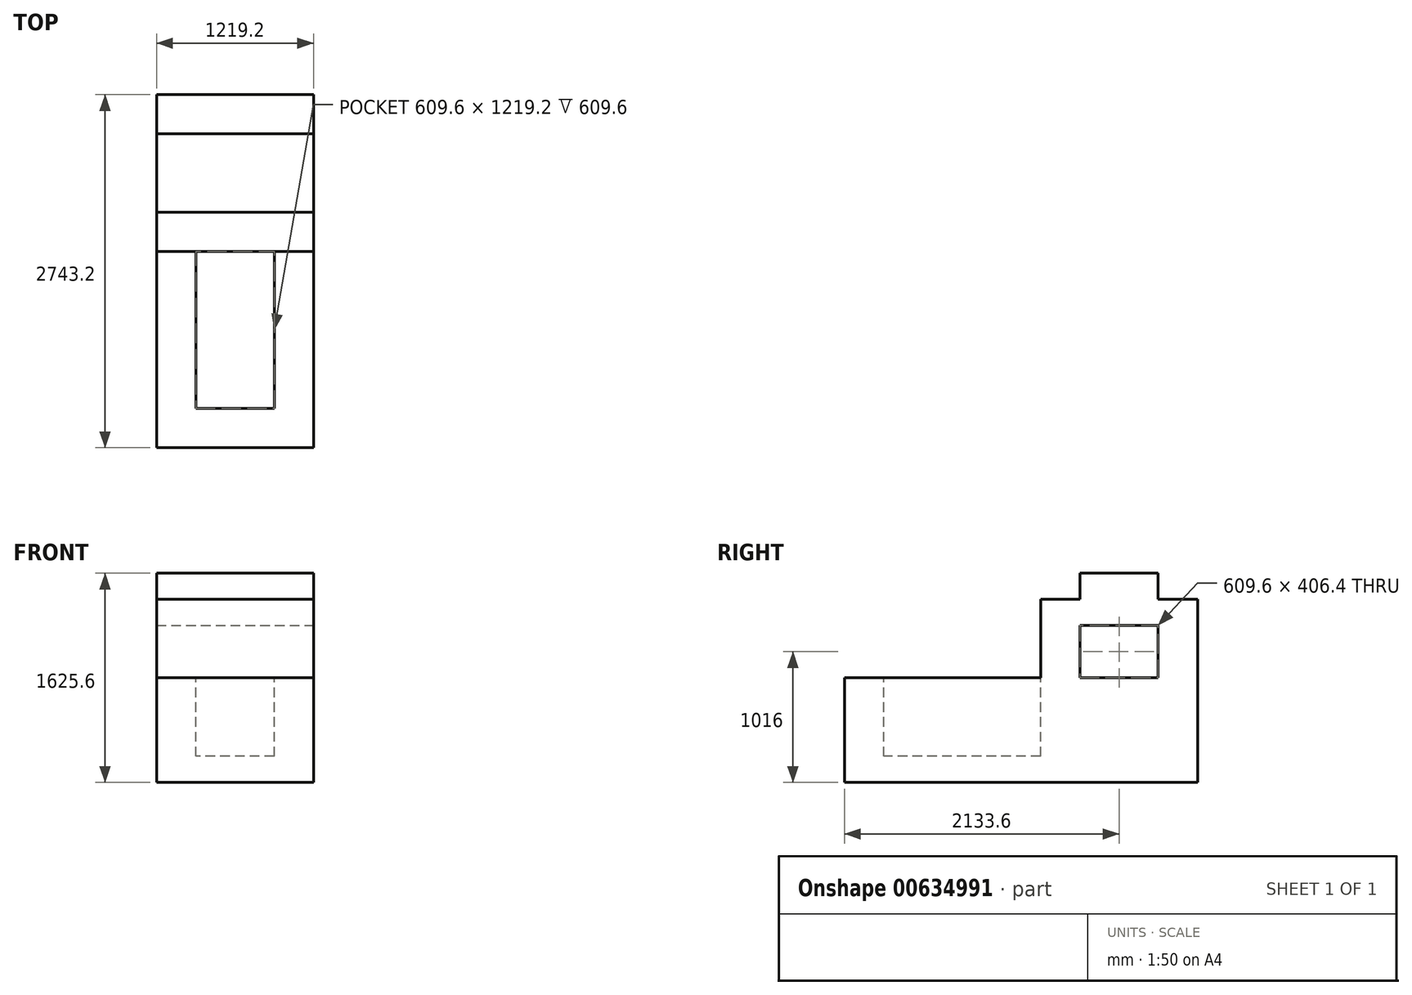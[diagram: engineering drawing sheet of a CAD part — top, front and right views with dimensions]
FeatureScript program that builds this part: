
annotation { "Feature Type Name" : "Feature", "Feature Type Description" : "" }
export const myFeature = defineFeature(function(context is Context, id is Id, definition is map)
    precondition{}
    {
        {
            var Q0;
            Q0=qCreatedBy(makeId("Right.planeOp"),FACE);
            var sketch = newSketch(context, id + "F0", { "sketchPlane" : qUnion([Q0])});
            skLineSegment(sketch, "E0", {"start": v(-227.36, -85.91) * mm, "end": v(2515.84, -85.91) * mm});
            skLineSegment(sketch, "E1", {"start": v(2515.84, -85.91) * mm, "end": v(2515.84, 1336.49) * mm});
            skLineSegment(sketch, "E2", {"start": v(2515.84, 1336.49) * mm, "end": v(2211.04, 1336.49) * mm});
            skLineSegment(sketch, "E3", {"start": v(2211.04, 1336.49) * mm, "end": v(2211.04, 1539.69) * mm});
            skLineSegment(sketch, "E4", {"start": v(2211.04, 1539.69) * mm, "end": v(1601.44, 1539.69) * mm});
            skLineSegment(sketch, "E5", {"start": v(1601.44, 1539.69) * mm, "end": v(1601.44, 1336.49) * mm});
            skLineSegment(sketch, "E6", {"start": v(1601.44, 1336.49) * mm, "end": v(1296.64, 1336.49) * mm});
            skLineSegment(sketch, "E7", {"start": v(1296.64, 1336.49) * mm, "end": v(1296.64, 726.89) * mm});
            skLineSegment(sketch, "E8", {"start": v(1296.64, 726.89) * mm, "end": v(-227.36, 726.89) * mm});
            skLineSegment(sketch, "E9", {"start": v(-227.36, 726.89) * mm, "end": v(-227.36, -85.91) * mm});
            skSolve(sketch);
        }
        {
            var Q0;
            Q0 = qSketchRegion(id + "F0", true);
            extrude(context, id + "F1", {"entities" : qUnion([Q0]), "depth" : 1219.2 * mm, "offsetDistance" : 25.4 * mm});
        }
        {
            var Q0;
            Q0=makeQuery(id+"F1.opExtrude","CAP_FACE",FACE,{"disambiguationData":[OSD([sQuery(id+"F0.wireOp",EDGE,"E0"),sQuery(id+"F0.wireOp",EDGE,"E1"),sQuery(id+"F0.wireOp",EDGE,"E2"),sQuery(id+"F0.wireOp",EDGE,"E3"),sQuery(id+"F0.wireOp",EDGE,"E4"),sQuery(id+"F0.wireOp",EDGE,"E5"),sQuery(id+"F0.wireOp",EDGE,"E6"),sQuery(id+"F0.wireOp",EDGE,"E7"),sQuery(id+"F0.wireOp",EDGE,"E8"),sQuery(id+"F0.wireOp",EDGE,"E9")])],"isStart":false});
            var sketch = newSketch(context, id + "F2", { "sketchPlane" : qUnion([Q0])});
            skLineSegment(sketch, "E10", {"start": v(2211.04, 1133.29) * mm, "end": v(1601.44, 1133.29) * mm});
            skLineSegment(sketch, "E11", {"start": v(1601.44, 1133.29) * mm, "end": v(1601.44, 726.89) * mm});
            skLineSegment(sketch, "E12", {"start": v(1601.44, 726.89) * mm, "end": v(2211.04, 726.89) * mm});
            skLineSegment(sketch, "E13", {"start": v(2211.04, 726.89) * mm, "end": v(2211.04, 1133.29) * mm});
            skSolve(sketch);
        }
        {
            var Q0;
            Q0 = qSketchRegion(id + "F2", true);
            extrude(context, id + "F3", {"entities" : qUnion([Q0]), "operationType" : NewBodyOperationType.REMOVE, "oppositeDirection" : true, "depth" : 1219.2 * mm, "offsetDistance" : 25.4 * mm});
        }
        {
            var Q0;
            Q0=makeQuery(id+"F1.opExtrude","SWEPT_FACE",FACE,{"disambiguationData":[OSD([sQuery(id+"F0.wireOp",EDGE,"E8")])]});
            var sketch = newSketch(context, id + "F4", { "sketchPlane" : qUnion([Q0])});
            skLineSegment(sketch, "E14", {"start": v(0, 1296.64) * mm, "end": v(304.8, 1296.64) * mm});
            skLineSegment(sketch, "E15", {"start": v(304.8, 1296.64) * mm, "end": v(304.8, 77.44) * mm});
            skLineSegment(sketch, "E16", {"start": v(304.8, 77.44) * mm, "end": v(914.4, 77.44) * mm});
            skLineSegment(sketch, "E17", {"start": v(914.4, 77.44) * mm, "end": v(914.4, 1296.64) * mm});
            skLineSegment(sketch, "E18", {"start": v(914.4, 1296.64) * mm, "end": v(304.8, 1296.64) * mm});
            skSolve(sketch);
        }
        {
            var Q0;
            Q0=makeQuery(id+"F4.imprint","IMPRINT",FACE,{"disambiguationData":[TD([[makeQuery(id+"F4.imprint","IMPRINT",EDGE,{"derivedFrom":sQuery(id+"F4.wireOp",EDGE,"E15")}),1.0]])]});
            extrude(context, id + "F5", {"entities" : qUnion([Q0]), "operationType" : NewBodyOperationType.REMOVE, "oppositeDirection" : true, "depth" : 609.6 * mm, "offsetDistance" : 25.4 * mm});
        }
    });
